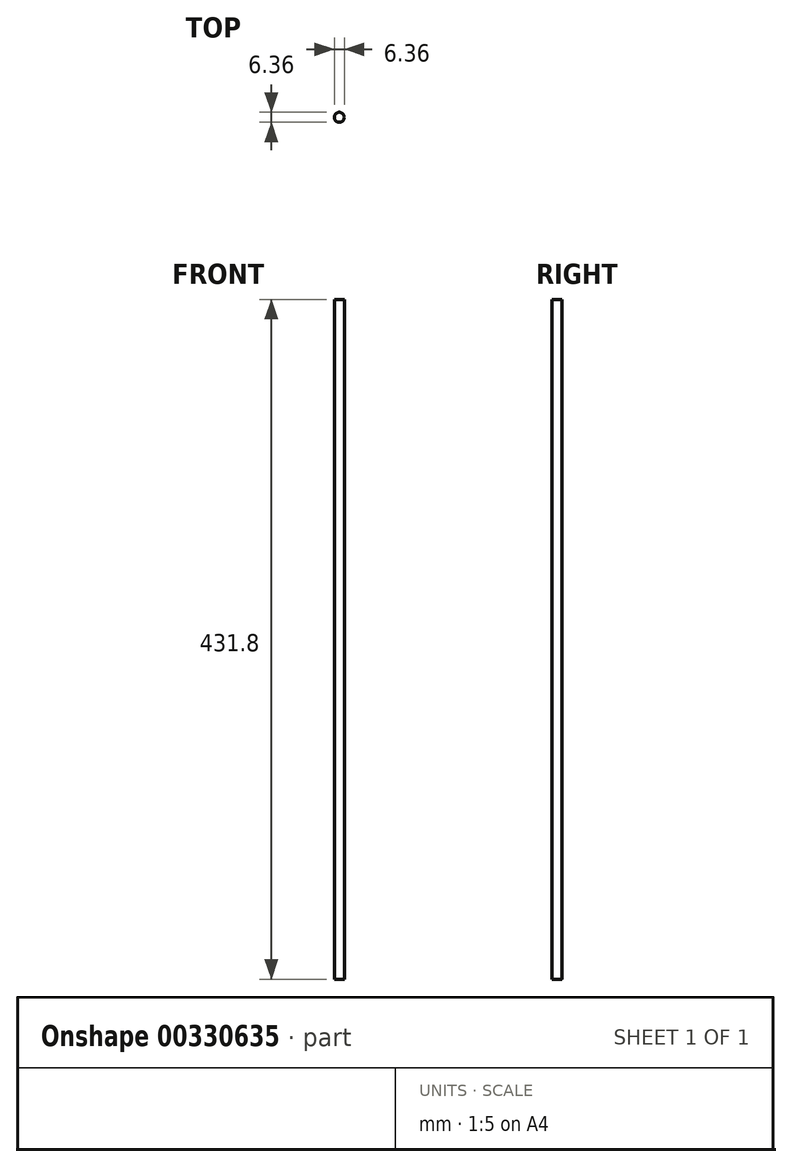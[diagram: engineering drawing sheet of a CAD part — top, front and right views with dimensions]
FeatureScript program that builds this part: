
annotation { "Feature Type Name" : "Feature", "Feature Type Description" : "" }
export const myFeature = defineFeature(function(context is Context, id is Id, definition is map)
    precondition{}
    {
        {
            var Q0;
            Q0=qCreatedBy(makeId("Top.planeOp"),FACE);
            var sketch = newSketch(context, id + "F0", { "sketchPlane" : qUnion([Q0])});
            skCircle(sketch, "E0", {"center": v(0, 0) * mm, "radius": 3.18 * mm});
            skSolve(sketch);
        }
        {
            var Q0;
            Q0=makeQuery(id+"F0.imprint","IMPRINT",FACE,{"disambiguationData":[TD([[makeQuery(id+"F0.imprint","IMPRINT",EDGE,{"derivedFrom":sQuery(id+"F0.wireOp",EDGE,"E0")}),1.0]])]});
            extrude(context, id + "F1", {"entities" : qUnion([Q0]), "endBound" : BoundingType.SYMMETRIC, "depth" : 431.8 * mm});
        }
    });
